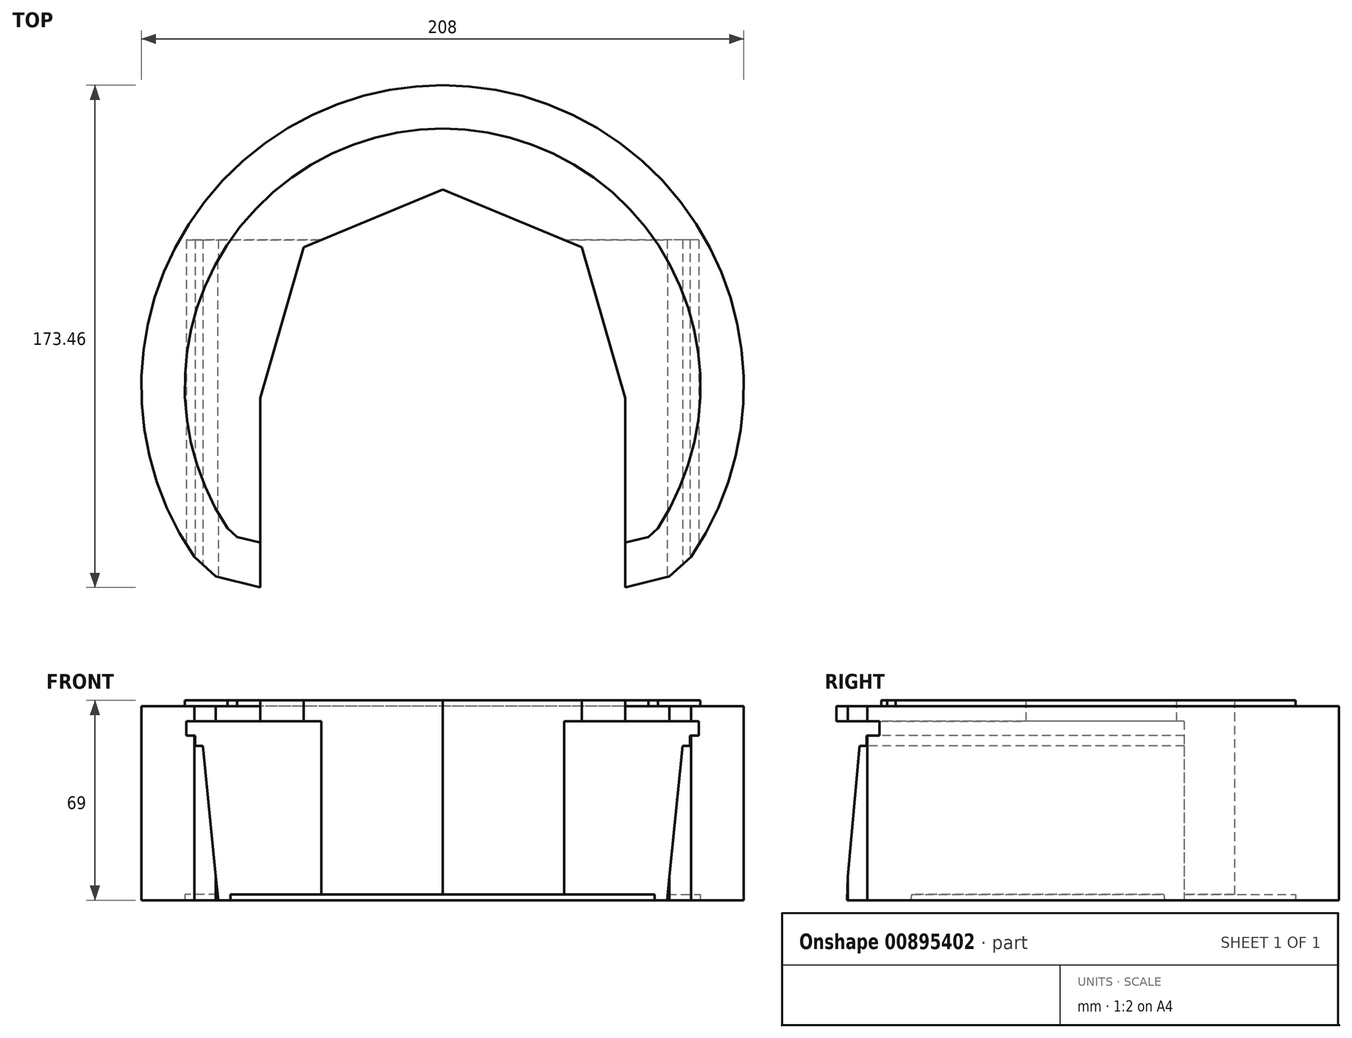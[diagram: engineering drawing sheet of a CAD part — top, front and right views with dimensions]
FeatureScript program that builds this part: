
annotation { "Feature Type Name" : "Feature", "Feature Type Description" : "" }
export const myFeature = defineFeature(function(context is Context, id is Id, definition is map)
    precondition{}
    {
        {
            var Q0;
            Q0=qCreatedBy(makeId("Top.planeOp"),FACE);
            var sketch = newSketch(context, id + "F0", { "sketchPlane" : qUnion([Q0])});
            skCircle(sketch, "E0", {"center": v(0, 0) * mm, "radius": 89 * mm});
            skLineSegment(sketch, "E1.bottom", {"start": v(89, 89) * mm, "end": v(-89, 89) * mm, "construction": true});
            skLineSegment(sketch, "E1.top", {"start": v(89, -89) * mm, "end": v(-89, -89) * mm, "construction": true});
            skLineSegment(sketch, "E1.left", {"start": v(89, 89) * mm, "end": v(89, -89) * mm, "construction": true});
            skLineSegment(sketch, "E1.right", {"start": v(-89, 89) * mm, "end": v(-89, -89) * mm, "construction": true});
            skLineSegment(sketch, "E2", {"start": v(-130.97, 89) * mm, "end": v(-130.97, -61) * mm, "construction": true});
            skLineSegment(sketch, "E3", {"start": v(-130.97, -61) * mm, "end": v(89, -61) * mm, "construction": true});
            skLineSegment(sketch, "E4", {"start": v(89, 0) * mm, "end": v(-130.97, 0) * mm, "construction": true});
            skPoint(sketch, "E4.endSnap0", {"position": v(-89, 0) * mm});
            skLineSegment(sketch, "E5", {"start": v(-130.97, -49) * mm, "end": v(89, -49) * mm, "construction": true});
            skLineSegment(sketch, "E6", {"start": v(-74.3, -49) * mm, "end": v(-74.3, 0) * mm, "construction": true});
            skLineSegment(sketch, "E7", {"start": v(-130.97, -52) * mm, "end": v(89, -52) * mm, "construction": true});
            skLineSegment(sketch, "E8", {"start": v(-71, -52) * mm, "end": v(-71, 0) * mm, "construction": true});
            skLineSegment(sketch, "E9", {"start": v(-74.3, -49) * mm, "end": v(-71, -52) * mm});
            skLineSegment(sketch, "E10", {"start": v(-130.97, -54) * mm, "end": v(89, -54) * mm});
            skLineSegment(sketch, "E11", {"start": v(-63, -54) * mm, "end": v(-63, 0) * mm, "construction": true});
            skLineSegment(sketch, "E12", {"start": v(-71, -52) * mm, "end": v(-63, -54) * mm});
            skLineSegment(sketch, "E13", {"start": v(-63, -54) * mm, "end": v(-63, -55.85) * mm});
            skLineSegment(sketch, "E14", {"start": v(0, -89) * mm, "end": v(0, 89) * mm, "construction": true});
            skLineSegment(sketch, "E15.MirrorCS", {"start": v(74.3, -49) * mm, "end": v(71, -52) * mm});
            skLineSegment(sketch, "E16.MirrorCS", {"start": v(71, -52) * mm, "end": v(63, -54) * mm});
            skLineSegment(sketch, "E17.MirrorCS", {"start": v(63, -54) * mm, "end": v(63, -55.85) * mm});
            skLineSegment(sketch, "E18", {"start": v(89, -59) * mm, "end": v(-89, -59) * mm, "construction": true});
            skPoint(sketch, "E19", {"position": v(0, -59) * mm});
            skArc(sketch, "E20", {"start": v(-63, -55.85) * mm, "mid": v(0, -59) * mm, "end": v(63, -55.85) * mm});
            skSolve(sketch);
        }
        {
            var Q0;
            {var subQ3=sQuery(id+"F0.wireOp",EDGE,"E9");Q0=makeQuery(id+"F0.imprint","IMPRINT",FACE,{"disambiguationData":[TD([[makeQuery(id+"F0.imprint","IMPRINT",EDGE,{"derivedFrom":subQ3}),1.0]])]});}
            var sketch = newSketch(context, id + "F1", { "sketchPlane" : qUnion([Q0])});
            skArc(sketch, "E21.0", {"start": v(74.3, -49) * mm, "mid": v(0, 89) * mm, "end": v(-74.3, -49) * mm});
            skLineSegment(sketch, "E22.0", {"start": v(-74.3, -49) * mm, "end": v(-71, -52) * mm});
            skLineSegment(sketch, "E23.0", {"start": v(-71, -52) * mm, "end": v(-63, -54) * mm});
            skLineSegment(sketch, "E24.0", {"start": v(-63, -54) * mm, "end": v(-63, -69.46) * mm});
            skLineSegment(sketch, "E25.0", {"start": v(74.3, -49) * mm, "end": v(71, -52) * mm});
            skLineSegment(sketch, "E26.0", {"start": v(71, -52) * mm, "end": v(63, -54) * mm});
            skLineSegment(sketch, "E27.0", {"start": v(63, -54) * mm, "end": v(63, -69.46) * mm});
            skLineSegment(sketch, "E28.0", {"start": v(-78.3, -65.64) * mm, "end": v(-63, -69.46) * mm});
            skLineSegment(sketch, "E28.1", {"start": v(78.3, -65.64) * mm, "end": v(63, -69.46) * mm});
            skLineSegment(sketch, "E28.2", {"start": v(85.73, -58.88) * mm, "end": v(78.3, -65.64) * mm});
            skArc(sketch, "E28.3", {"start": v(85.73, -58.88) * mm, "mid": v(0, 104) * mm, "end": v(-85.73, -58.88) * mm});
            skLineSegment(sketch, "E28.4", {"start": v(-85.73, -58.88) * mm, "end": v(-78.3, -65.64) * mm});
            skPoint(sketch, "E29.orphan", {"position": v(63, -55.85) * mm});
            skPoint(sketch, "E30.orphan", {"position": v(-63, -55.85) * mm});
            skSolve(sketch);
        }
        {
            var Q0;
            Q0 = qSketchRegion(id + "F1", true);
            extrude(context, id + "F2", {"entities" : qUnion([Q0]), "depth" : 2 * mm, "offsetDistance" : 25 * mm});
        }
        {
            var Q0;
            Q0=makeQuery(id+"F2.opExtrude","CAP_FACE",FACE,{"disambiguationData":[OSD([sQuery(id+"F1.wireOp",EDGE,"E21.0"),sQuery(id+"F1.wireOp",EDGE,"E22.0"),sQuery(id+"F1.wireOp",EDGE,"E23.0"),sQuery(id+"F1.wireOp",EDGE,"E24.0"),sQuery(id+"F1.wireOp",EDGE,"E25.0"),sQuery(id+"F1.wireOp",EDGE,"E26.0"),sQuery(id+"F1.wireOp",EDGE,"E27.0"),sQuery(id+"F1.wireOp",EDGE,"E28.0"),sQuery(id+"F1.wireOp",EDGE,"E28.1"),sQuery(id+"F1.wireOp",EDGE,"E28.2"),sQuery(id+"F1.wireOp",EDGE,"E28.3"),sQuery(id+"F1.wireOp",EDGE,"E28.4")])],"isStart":false});
            var sketch = newSketch(context, id + "F3", { "sketchPlane" : qUnion([Q0])});
            skLineSegment(sketch, "E31", {"start": v(-63, -69.46) * mm, "end": v(63, -69.46) * mm});
            skLineSegment(sketch, "E32.0", {"start": v(-78.3, -65.64) * mm, "end": v(-63, -69.46) * mm});
            skLineSegment(sketch, "E33.0", {"start": v(-85.73, -58.88) * mm, "end": v(-78.3, -65.64) * mm});
            skArc(sketch, "E34.0", {"start": v(85.73, -58.88) * mm, "mid": v(0, 104) * mm, "end": v(-85.73, -58.88) * mm});
            skLineSegment(sketch, "E35.0", {"start": v(85.73, -58.88) * mm, "end": v(78.3, -65.64) * mm});
            skLineSegment(sketch, "E36.0", {"start": v(78.3, -65.64) * mm, "end": v(63, -69.46) * mm});
            skSolve(sketch);
        }
        {
            var Q0;
            Q0 = qSketchRegion(id + "F3", true);
            extrude(context, id + "F4", {"entities" : qUnion([Q0]), "operationType" : NewBodyOperationType.ADD, "depth" : 65 * mm, "offsetDistance" : 25 * mm});
        }
        {
            var Q0;
            Q0=makeQuery(id+"F4.opExtrude","CAP_FACE",FACE,{"disambiguationData":[OSD([sQuery(id+"F3.wireOp",EDGE,"E31"),sQuery(id+"F3.wireOp",EDGE,"E32.0"),sQuery(id+"F3.wireOp",EDGE,"E33.0"),sQuery(id+"F3.wireOp",EDGE,"E34.0"),sQuery(id+"F3.wireOp",EDGE,"E35.0"),sQuery(id+"F3.wireOp",EDGE,"E36.0")])],"isStart":false});
            var sketch = newSketch(context, id + "F5", { "sketchPlane" : qUnion([Q0])});
            skLineSegment(sketch, "E37.0", {"start": v(71, -52) * mm, "end": v(63, -54) * mm});
            skLineSegment(sketch, "E38.0.1", {"start": v(63, -54) * mm, "end": v(63, -69.46) * mm});
            skLineSegment(sketch, "E38.0.2", {"start": v(63, -69.46) * mm, "end": v(-63, -69.46) * mm});
            skLineSegment(sketch, "E38.0.3", {"start": v(-63, -69.46) * mm, "end": v(-63, -54) * mm});
            skLineSegment(sketch, "E38.0.4", {"start": v(-63, -54) * mm, "end": v(-71, -52) * mm});
            skLineSegment(sketch, "E38.0.5", {"start": v(-71, -52) * mm, "end": v(-74.3, -49) * mm});
            skArc(sketch, "E38.0.6", {"start": v(-74.3, -49) * mm, "mid": v(0, 89) * mm, "end": v(74.3, -49) * mm});
            skLineSegment(sketch, "E38.0.7", {"start": v(74.3, -49) * mm, "end": v(71, -52) * mm});
            skSolve(sketch);
        }
        {
            var Q0;
            Q0 = qSketchRegion(id + "F5", true);
            extrude(context, id + "F6", {"entities" : qUnion([Q0]), "operationType" : NewBodyOperationType.ADD, "depth" : 2 * mm, "offsetDistance" : 25 * mm});
        }
        {
            var Q0;
            Q0=makeQuery(id+"F6.boolean.opBoolean","MERGE",FACE,{"derivedFrom":[makeQuery(id+"F4.opExtrude","SWEPT_FACE",FACE,{"disambiguationData":[OSD([sQuery(id+"F3.wireOp",EDGE,"E31")])]}),makeQuery(id+"F6.opExtrude","SWEPT_FACE",FACE,{"disambiguationData":[OSD([sQuery(id+"F5.wireOp",EDGE,"E38.0.2")])]})]});
            var sketch = newSketch(context, id + "F7", { "sketchPlane" : qUnion([Q0])});
            skLineSegment(sketch, "E39.bottom", {"start": v(88.5, 61.83) * mm, "end": v(-88.5, 61.83) * mm});
            skLineSegment(sketch, "E40", {"start": v(0, 61.83) * mm, "end": v(0, 1.83) * mm, "construction": true});
            skLineSegment(sketch, "E41", {"start": v(82.8, 53.33) * mm, "end": v(77.28, -2) * mm});
            skLineSegment(sketch, "E42", {"start": v(-77.28, -2) * mm, "end": v(77.28, -2) * mm});
            skLineSegment(sketch, "E43", {"start": v(88.5, 61.83) * mm, "end": v(88.5, 56.83) * mm});
            skLineSegment(sketch, "E44", {"start": v(88.5, 56.83) * mm, "end": v(85.44, 56.83) * mm});
            skLineSegment(sketch, "E45", {"start": v(85.44, 56.83) * mm, "end": v(85.44, 53.33) * mm});
            skLineSegment(sketch, "E46", {"start": v(85.44, 53.33) * mm, "end": v(82.8, 53.33) * mm});
            skLineSegment(sketch, "E47.MirrorCS", {"start": v(-82.8, 53.33) * mm, "end": v(-77.28, -2) * mm});
            skLineSegment(sketch, "E48.MirrorCS", {"start": v(-85.44, 53.33) * mm, "end": v(-82.8, 53.33) * mm});
            skLineSegment(sketch, "E49.MirrorCS", {"start": v(-85.44, 56.83) * mm, "end": v(-85.44, 53.33) * mm});
            skLineSegment(sketch, "E50.MirrorCS", {"start": v(-88.5, 56.83) * mm, "end": v(-85.44, 56.83) * mm});
            skLineSegment(sketch, "E51.MirrorCS", {"start": v(-88.5, 61.83) * mm, "end": v(-88.5, 56.83) * mm});
            skLineSegment(sketch, "E52", {"start": v(0, 0) * mm, "end": v(0, 5.84) * mm, "construction": true});
            skSolve(sketch);
        }
        {
            var Q0;
            Q0 = qSketchRegion(id + "F7", true);
            var Q1;
            Q1=sQuery(id+"F7.wireOp",EDGE,"E39.bottom");
            var Q2;
            Q2=sQuery(id+"F7.wireOp",EDGE,"uddJmaR7-9RPt-Evpt-hBqF-c7Tb3bwEk4kM");
            var Q3;
            Q3=sQuery(id+"F7.wireOp",EDGE,"E42");
            var Q4;
            Q4=sQuery(id+"F7.wireOp",EDGE,"E41");
            extrude(context, id + "F8", {"entities" : qUnion([Q0]), "operationType" : NewBodyOperationType.REMOVE, "surfaceEntities" : qUnion([Q1, Q2, Q3, Q4]), "depth" : 25 * mm, "offsetDistance" : 25 * mm});
        }
        {
            var Q0;
            Q0 = qSketchRegion(id + "F7", true);
            extrude(context, id + "F9", {"entities" : qUnion([Q0]), "operationType" : NewBodyOperationType.REMOVE, "oppositeDirection" : true, "depth" : 120 * mm, "offsetDistance" : 25 * mm});
        }
        {
            var Q0;
            Q0=makeQuery(id+"F6.opExtrude","CAP_FACE",FACE,{"disambiguationData":[OSD([sQuery(id+"F5.wireOp",EDGE,"E37.0"),sQuery(id+"F5.wireOp",EDGE,"E38.0.1"),sQuery(id+"F5.wireOp",EDGE,"E38.0.2"),sQuery(id+"F5.wireOp",EDGE,"E38.0.3"),sQuery(id+"F5.wireOp",EDGE,"E38.0.4"),sQuery(id+"F5.wireOp",EDGE,"E38.0.5"),sQuery(id+"F5.wireOp",EDGE,"E38.0.6"),sQuery(id+"F5.wireOp",EDGE,"E38.0.7")])],"isStart":false});
            var sketch = newSketch(context, id + "F10", { "sketchPlane" : qUnion([Q0])});
            skLineSegment(sketch, "E53", {"start": v(0, 89) * mm, "end": v(0, -69.46) * mm, "construction": true});
            skLineSegment(sketch, "E54", {"start": v(-63, -54) * mm, "end": v(-63, -4) * mm});
            skLineSegment(sketch, "E55", {"start": v(-63, -4) * mm, "end": v(-48, -4) * mm, "construction": true});
            skLineSegment(sketch, "E56", {"start": v(-48, -4) * mm, "end": v(-48, 48) * mm, "construction": true});
            skLineSegment(sketch, "E57", {"start": v(-48, 48) * mm, "end": v(0, 48) * mm, "construction": true});
            skLineSegment(sketch, "E58", {"start": v(0, 48) * mm, "end": v(0, 68) * mm, "construction": true});
            skLineSegment(sketch, "E59", {"start": v(0, 68) * mm, "end": v(-48, 48) * mm});
            skLineSegment(sketch, "E60", {"start": v(-48, 48) * mm, "end": v(-63, -4) * mm});
            skLineSegment(sketch, "E61", {"start": v(-63, -54) * mm, "end": v(-63, -69.46) * mm});
            skLineSegment(sketch, "E62", {"start": v(-63, -69.46) * mm, "end": v(0, -69.46) * mm});
            skLineSegment(sketch, "E63.MirrorCS", {"start": v(0, 68) * mm, "end": v(48, 48) * mm});
            skLineSegment(sketch, "E64.MirrorCS", {"start": v(48, 48) * mm, "end": v(63, -4) * mm});
            skLineSegment(sketch, "E65.MirrorCS", {"start": v(63, -54) * mm, "end": v(63, -4) * mm});
            skLineSegment(sketch, "E66.MirrorCS", {"start": v(63, -54) * mm, "end": v(63, -69.46) * mm});
            skLineSegment(sketch, "E67.MirrorCS", {"start": v(63, -69.46) * mm, "end": v(0, -69.46) * mm});
            skSolve(sketch);
        }
        {
            var Q0;
            Q0 = qSketchRegion(id + "F10", true);
            extrude(context, id + "F11", {"entities" : qUnion([Q0]), "operationType" : NewBodyOperationType.REMOVE, "endBound" : BoundingType.THROUGH_ALL, "oppositeDirection" : true, "depth" : 25 * mm, "offsetDistance" : 25 * mm});
        }
    });
